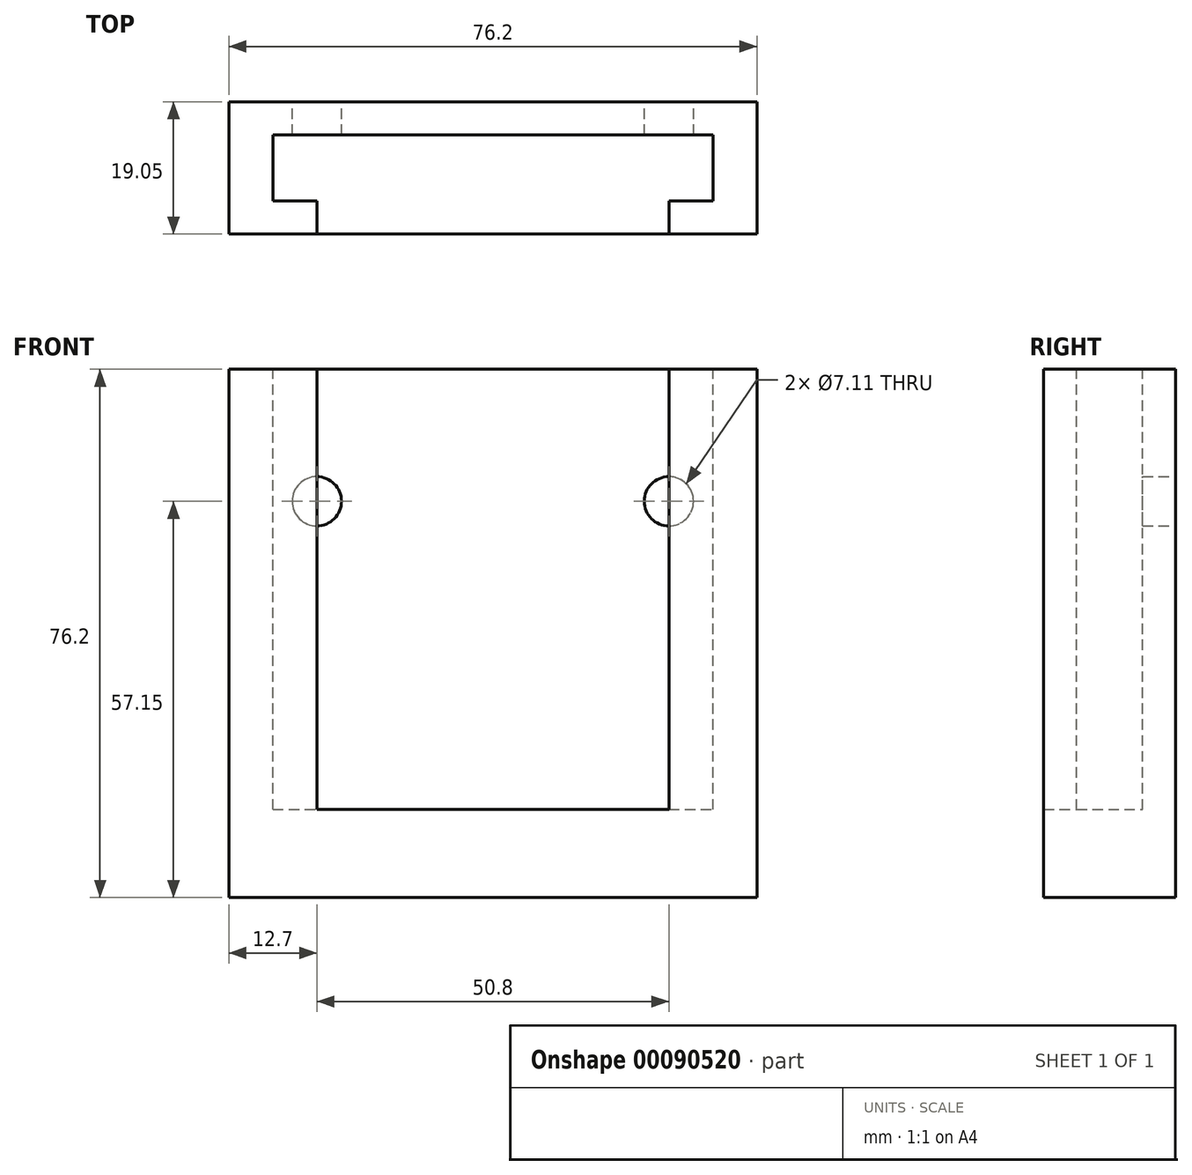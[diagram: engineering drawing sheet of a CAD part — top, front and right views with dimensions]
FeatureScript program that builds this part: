
annotation { "Feature Type Name" : "Feature", "Feature Type Description" : "" }
export const myFeature = defineFeature(function(context is Context, id is Id, definition is map)
    precondition{}
    {
        {
            var Q0;
            Q0=qCreatedBy(makeId("Front.planeOp"),FACE);
            var sketch = newSketch(context, id + "F0", { "sketchPlane" : qUnion([Q0])});
            skLineSegment(sketch, "E0", {"start": v(0, 0) * mm, "end": v(0, 38.1) * mm});
            skLineSegment(sketch, "E1", {"start": v(0, 0) * mm, "end": v(0, -38.1) * mm});
            skLineSegment(sketch, "E2", {"start": v(-38.1, 0) * mm, "end": v(-38.1, 38.1) * mm});
            skLineSegment(sketch, "E3", {"start": v(-38.1, 38.1) * mm, "end": v(38.1, 38.1) * mm});
            skLineSegment(sketch, "E4", {"start": v(38.1, 0) * mm, "end": v(38.1, 38.1) * mm});
            skLineSegment(sketch, "E5", {"start": v(38.1, 0) * mm, "end": v(38.1, -38.1) * mm});
            skLineSegment(sketch, "E6", {"start": v(38.1, -38.1) * mm, "end": v(-38.1, -38.1) * mm});
            skLineSegment(sketch, "E7", {"start": v(-38.1, 0) * mm, "end": v(-38.1, -38.1) * mm});
            skSolve(sketch);
        }
        {
            var Q0;
            Q0=qSketchRegion(id+"F0",true);
            extrude(context, id + "F1", {"entities" : qUnion([Q0]), "depth" : 19.05 * mm});
        }
        {
            var Q0;
            Q0=makeQuery(id+"F1.opExtrude","SWEPT_FACE",FACE,{"disambiguationData":[OSD([sQuery(id+"F0.wireOp",EDGE,"E3")])]});
            var sketch = newSketch(context, id + "F2", { "sketchPlane" : qUnion([Q0])});
            skLineSegment(sketch, "E8", {"start": v(-38.1, -19.05) * mm, "end": v(-25.4, -19.05) * mm});
            skLineSegment(sketch, "E9", {"start": v(38.1, -19.05) * mm, "end": v(25.4, -19.05) * mm});
            skLineSegment(sketch, "E10", {"start": v(25.4, -19.05) * mm, "end": v(25.4, 0) * mm});
            skLineSegment(sketch, "E11", {"start": v(25.4, -9.53) * mm, "end": v(31.75, -9.53) * mm});
            skLineSegment(sketch, "E12", {"start": v(25.4, -9.53) * mm, "end": v(25.4, 0) * mm});
            skLineSegment(sketch, "E13", {"start": v(25.4, -4.76) * mm, "end": v(31.75, -4.76) * mm});
            skLineSegment(sketch, "E14", {"start": v(31.75, -4.76) * mm, "end": v(31.75, -9.53) * mm});
            skLineSegment(sketch, "E15", {"start": v(25.4, -9.53) * mm, "end": v(25.4, -19.05) * mm});
            skLineSegment(sketch, "E16", {"start": v(25.4, -14.29) * mm, "end": v(31.75, -14.29) * mm});
            skLineSegment(sketch, "E17", {"start": v(31.75, -14.29) * mm, "end": v(31.75, -9.53) * mm});
            skLineSegment(sketch, "E18.MirrorCS", {"start": v(-25.4, -19.05) * mm, "end": v(-25.4, 0) * mm});
            skLineSegment(sketch, "E19.MirrorCS", {"start": v(-25.4, -9.53) * mm, "end": v(-31.75, -9.53) * mm});
            skLineSegment(sketch, "E20.MirrorCS", {"start": v(-31.75, -14.29) * mm, "end": v(-31.75, -9.53) * mm});
            skLineSegment(sketch, "E21.MirrorCS", {"start": v(-25.4, -9.53) * mm, "end": v(-25.4, 0) * mm});
            skLineSegment(sketch, "E22.MirrorCS", {"start": v(-25.4, -4.76) * mm, "end": v(-31.75, -4.76) * mm});
            skLineSegment(sketch, "E23.MirrorCS", {"start": v(-25.4, -14.29) * mm, "end": v(-31.75, -14.29) * mm});
            skLineSegment(sketch, "E24.MirrorCS", {"start": v(-25.4, -9.53) * mm, "end": v(-25.4, -19.05) * mm});
            skLineSegment(sketch, "E25.MirrorCS", {"start": v(-31.75, -4.76) * mm, "end": v(-31.75, -9.53) * mm});
            skLineSegment(sketch, "E26", {"start": v(-31.75, -4.76) * mm, "end": v(31.75, -4.76) * mm});
            skLineSegment(sketch, "E27", {"start": v(31.75, -14.29) * mm, "end": v(-31.75, -14.29) * mm});
            skSolve(sketch);
        }
        {
            var Q0;
            Q0=qSketchRegion(id+"F2",true);
            var Q1;
            {var subQ0=sQuery(id+"F2.wireOp",EDGE,"E15");var subQ3=sQuery(id+"F2.wireOp",EDGE,"E27");var subQ4=makeQuery(id+"F2.imprint","INTERSECT",VERTEX,{"derivedFrom":[subQ0,subQ3]});Q1=makeQuery(id+"F2.imprint","IMPRINT",FACE,{"disambiguationData":[TD([[makeQuery(id+"F2.imprint","IMPRINT",EDGE,{"disambiguationData":[TD([[subQ4,-1.0]])],"derivedFrom":subQ3}),1.0]])]});}
            extrude(context, id + "F3", {"entities" : qUnion([Q0, Q1]), "operationType" : NewBodyOperationType.REMOVE, "oppositeDirection" : true, "depth" : 63.5 * mm});
        }
        {
            var Q0;
            Q0=makeQuery(id+"F1.opExtrude","CAP_FACE",FACE,{"disambiguationData":[OSD([sQuery(id+"F0.wireOp",EDGE,"E2"),sQuery(id+"F0.wireOp",EDGE,"E3"),sQuery(id+"F0.wireOp",EDGE,"E4"),sQuery(id+"F0.wireOp",EDGE,"E5"),sQuery(id+"F0.wireOp",EDGE,"E6"),sQuery(id+"F0.wireOp",EDGE,"E7")])],"isStart":true});
            var sketch = newSketch(context, id + "F4", { "sketchPlane" : qUnion([Q0])});
            skLineSegment(sketch, "E28", {"start": v(0, 0) * mm, "end": v(0, 38.1) * mm});
            skLineSegment(sketch, "E29", {"start": v(0, 38.1) * mm, "end": v(0, 19.05) * mm});
            skLineSegment(sketch, "E30", {"start": v(0, 19.05) * mm, "end": v(-38.1, 19.05) * mm});
            skLineSegment(sketch, "E31", {"start": v(0, 19.05) * mm, "end": v(38.1, 19.05) * mm});
            skLineSegment(sketch, "E32", {"start": v(38.1, 19.05) * mm, "end": v(25.4, 19.05) * mm});
            skLineSegment(sketch, "E33", {"start": v(-38.1, 19.05) * mm, "end": v(-25.4, 19.05) * mm});
            skCircle(sketch, "E34", {"center": v(-25.4, 19.05) * mm, "radius": 3.56 * mm});
            skCircle(sketch, "E35", {"center": v(25.4, 19.05) * mm, "radius": 3.56 * mm});
            skSolve(sketch);
        }
        {
            var Q0;
            Q0=qSketchRegion(id+"F4",true);
            extrude(context, id + "F5", {"entities" : qUnion([Q0]), "operationType" : NewBodyOperationType.REMOVE, "oppositeDirection" : true, "depth" : 10.16 * mm});
        }
    });
